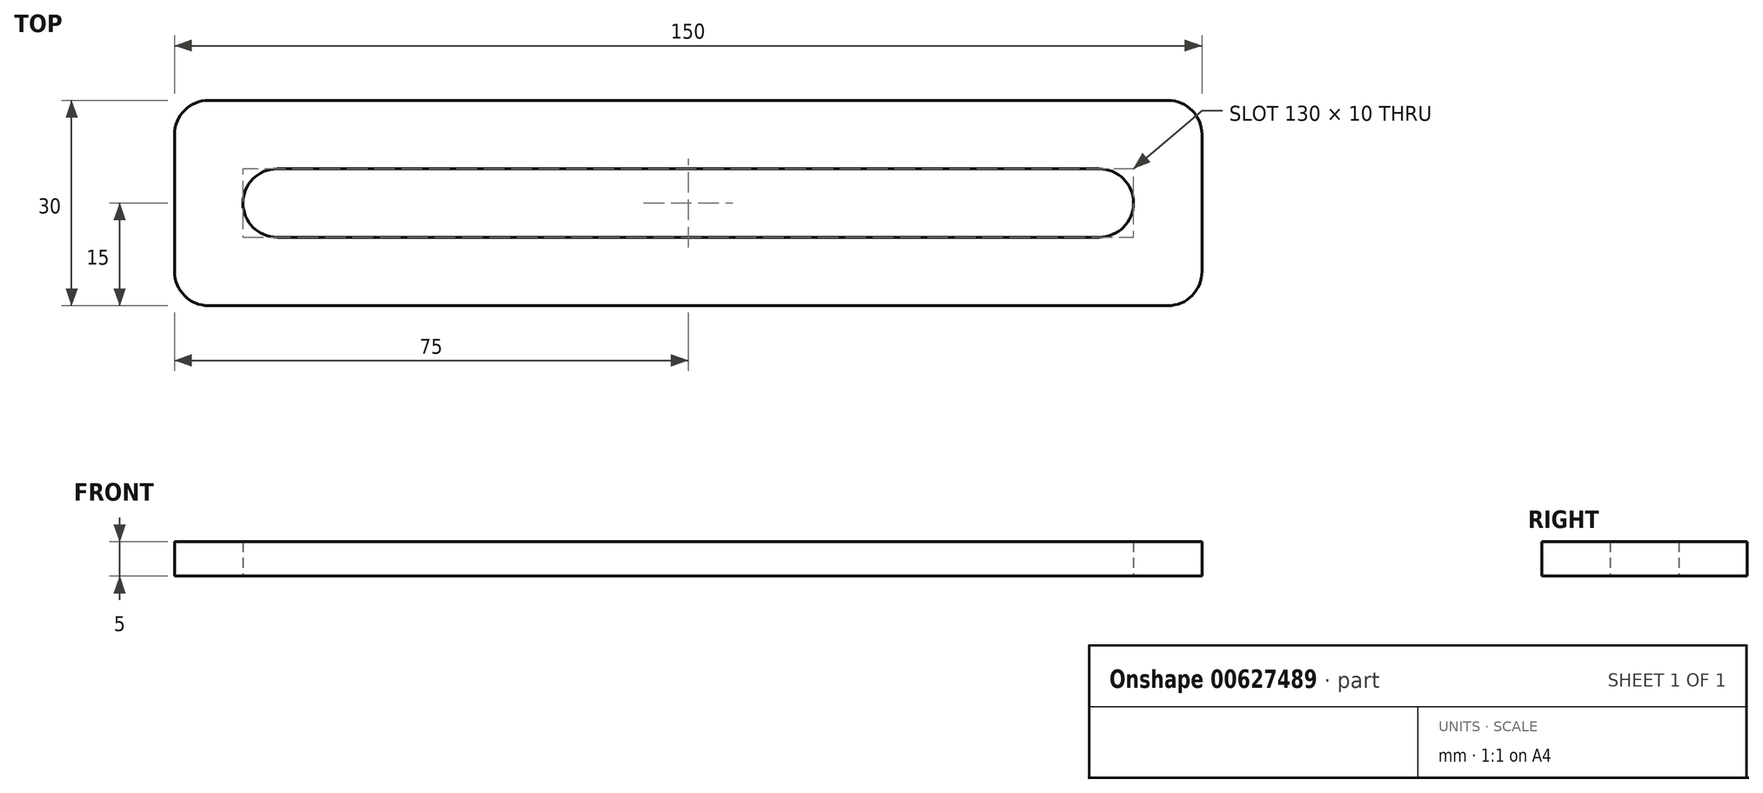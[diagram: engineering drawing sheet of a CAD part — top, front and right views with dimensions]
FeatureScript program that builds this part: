
annotation { "Feature Type Name" : "Feature", "Feature Type Description" : "" }
export const myFeature = defineFeature(function(context is Context, id is Id, definition is map)
    precondition{}
    {
        {
            var Q0;
            Q0=qCreatedBy(makeId("Top.planeOp"),FACE);
            var sketch = newSketch(context, id + "F0", { "sketchPlane" : qUnion([Q0])});
            skLineSegment(sketch, "E0.bottom", {"start": v(-70, 15) * mm, "end": v(70, 15) * mm});
            skLineSegment(sketch, "E0.top", {"start": v(-70, -15) * mm, "end": v(70, -15) * mm});
            skLineSegment(sketch, "E0.left", {"start": v(-75, 10) * mm, "end": v(-75, -10) * mm});
            skLineSegment(sketch, "E0.right", {"start": v(75, 10) * mm, "end": v(75, -10) * mm});
            skPoint(sketch, "E0.middle", {"position": v(0, 0) * mm});
            skArc(sketch, "E1", {"start": v(-60, 5) * mm, "mid": v(-65, 0) * mm, "end": v(-60, -5) * mm});
            skArc(sketch, "E2.MirrorC", {"start": v(60, 5) * mm, "mid": v(65, 0) * mm, "end": v(60, -5) * mm});
            skLineSegment(sketch, "E3", {"start": v(-60, 5) * mm, "end": v(60, 5) * mm});
            skLineSegment(sketch, "E4", {"start": v(60, -5) * mm, "end": v(-60, -5) * mm});
            skPoint(sketch, "E5.visualSharp", {"position": v(-75, 15) * mm});
            skArc(sketch, "E5.filletArc", {"start": v(-70, 15) * mm, "mid": v(-73.54, 13.54) * mm, "end": v(-75, 10) * mm});
            skPoint(sketch, "E6.visualSharp", {"position": v(-75, -15) * mm});
            skArc(sketch, "E6.filletArc", {"start": v(-75, -10) * mm, "mid": v(-73.54, -13.54) * mm, "end": v(-70, -15) * mm});
            skPoint(sketch, "E7.visualSharp", {"position": v(75, 15) * mm});
            skArc(sketch, "E7.filletArc", {"start": v(75, 10) * mm, "mid": v(73.54, 13.54) * mm, "end": v(70, 15) * mm});
            skPoint(sketch, "E8.visualSharp", {"position": v(75, -15) * mm});
            skArc(sketch, "E8.filletArc", {"start": v(70, -15) * mm, "mid": v(73.54, -13.54) * mm, "end": v(75, -10) * mm});
            skSolve(sketch);
        }
        {
            var Q0;
            Q0 = qSketchRegion(id + "F0", true);
            extrude(context, id + "F1", {"entities" : qUnion([Q0]), "depth" : 5 * mm, "offsetDistance" : 25 * mm});
        }
    });
